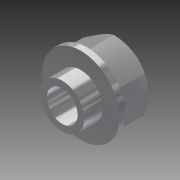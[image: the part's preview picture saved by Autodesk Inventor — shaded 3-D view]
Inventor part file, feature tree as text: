
AUTODESK INVENTOR PART (.ipt)
format: ipt  version: 2014 SP1 (Build 180222100, 222)  size: 120,320 bytes
history: native  units: in
note: dims shown in document units (in); Inventor stores cm internally (conversion verified against a paired STEP export)
features: sketch x5, extrude x4, revolve x1
ambient origin geometry x8: Origin, YZ Plane, XZ Plane, XY Plane, X Axis, Y Axis, Z Axis, Center Point
bodies: Solid1 (feature_tree)
feature tree (10):
  extrude  "Extrusion1"  Depth=0.1969in TaperAngle=0.0deg
  extrude  "Extrusion2"  Depth=0.0394in TaperAngle=0.0deg
  extrude  "Extrusion3"  Depth=0.1181in TaperAngle=0.0deg
  extrude  "Extrusion4"  Depth=0.1575in TaperAngle=0.0deg
  revolve  "Revolution1"  [1 undecoded]
  sketch  "Sketch1"  dims[d0=0.3937in d1=0.1969in d2=0.0in]
  sketch  "Sketch2"  dims[d3=0.4921in d4=0.0394in d5=0.0in]
  sketch  "Sketch3"  dims[d6=0.2803in d7=0.1181in d8=0.0in]
  sketch  "Sketch4"  dims[d9=0.1969in d10=0.1575in d11=0.0in]
  sketch  "Sketch5"  dims[d12=90.0deg]
note: 1 required parameter value undecoded (feature->parameter linkage not recoverable at this tier; creation-order binding heuristic only, values carry confidence <= 0.55)
